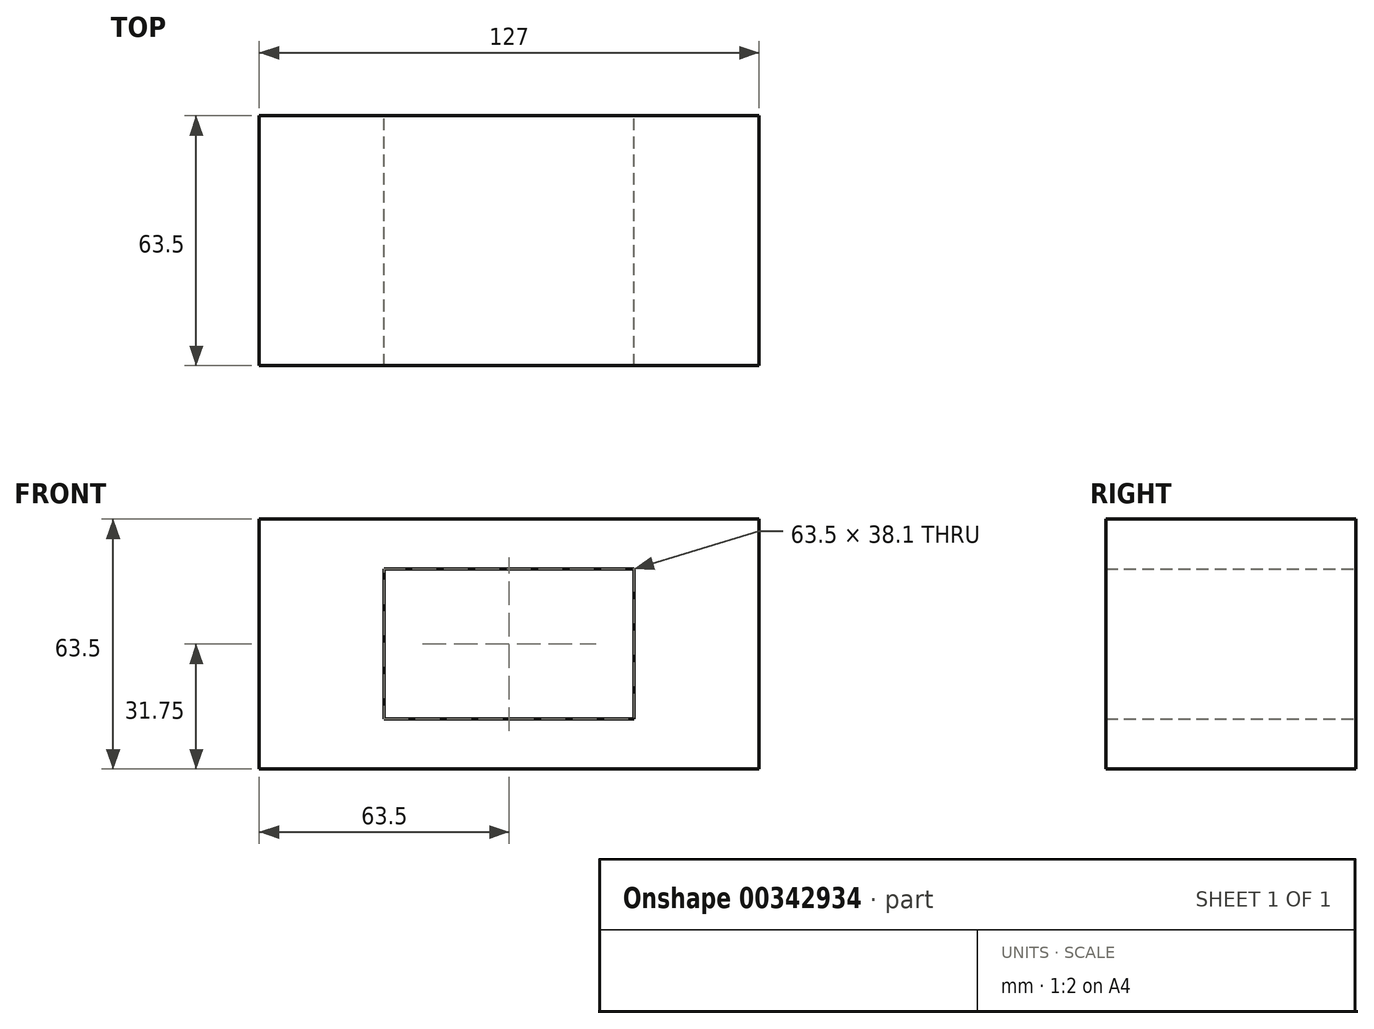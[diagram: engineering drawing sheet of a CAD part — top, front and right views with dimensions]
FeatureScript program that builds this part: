
annotation { "Feature Type Name" : "Feature", "Feature Type Description" : "" }
export const myFeature = defineFeature(function(context is Context, id is Id, definition is map)
    precondition{}
    {
        {
            var Q0;
            Q0=qCreatedBy(makeId("Front.planeOp"),FACE);
            var sketch = newSketch(context, id + "F0", { "sketchPlane" : qUnion([Q0])});
            skLineSegment(sketch, "E0.bottom", {"start": v(63.5, -31.75) * mm, "end": v(-63.5, -31.75) * mm});
            skLineSegment(sketch, "E0.top", {"start": v(63.5, 31.75) * mm, "end": v(-63.5, 31.75) * mm});
            skLineSegment(sketch, "E0.left", {"start": v(63.5, -31.75) * mm, "end": v(63.5, 31.75) * mm});
            skLineSegment(sketch, "E0.right", {"start": v(-63.5, -31.75) * mm, "end": v(-63.5, 31.75) * mm});
            skPoint(sketch, "E0.middle", {"position": v(0, 0) * mm});
            skLineSegment(sketch, "E1.bottom", {"start": v(31.75, -19.05) * mm, "end": v(-31.75, -19.05) * mm});
            skLineSegment(sketch, "E1.top", {"start": v(31.75, 19.05) * mm, "end": v(-31.75, 19.05) * mm});
            skLineSegment(sketch, "E1.left", {"start": v(31.75, -19.05) * mm, "end": v(31.75, 19.05) * mm});
            skLineSegment(sketch, "E1.right", {"start": v(-31.75, -19.05) * mm, "end": v(-31.75, 19.05) * mm});
            skSolve(sketch);
        }
        {
            var Q0;
            Q0 = qSketchRegion(id + "F0", true);
            extrude(context, id + "F1", {"entities" : qUnion([Q0]), "depth" : 63.5 * mm});
        }
    });
